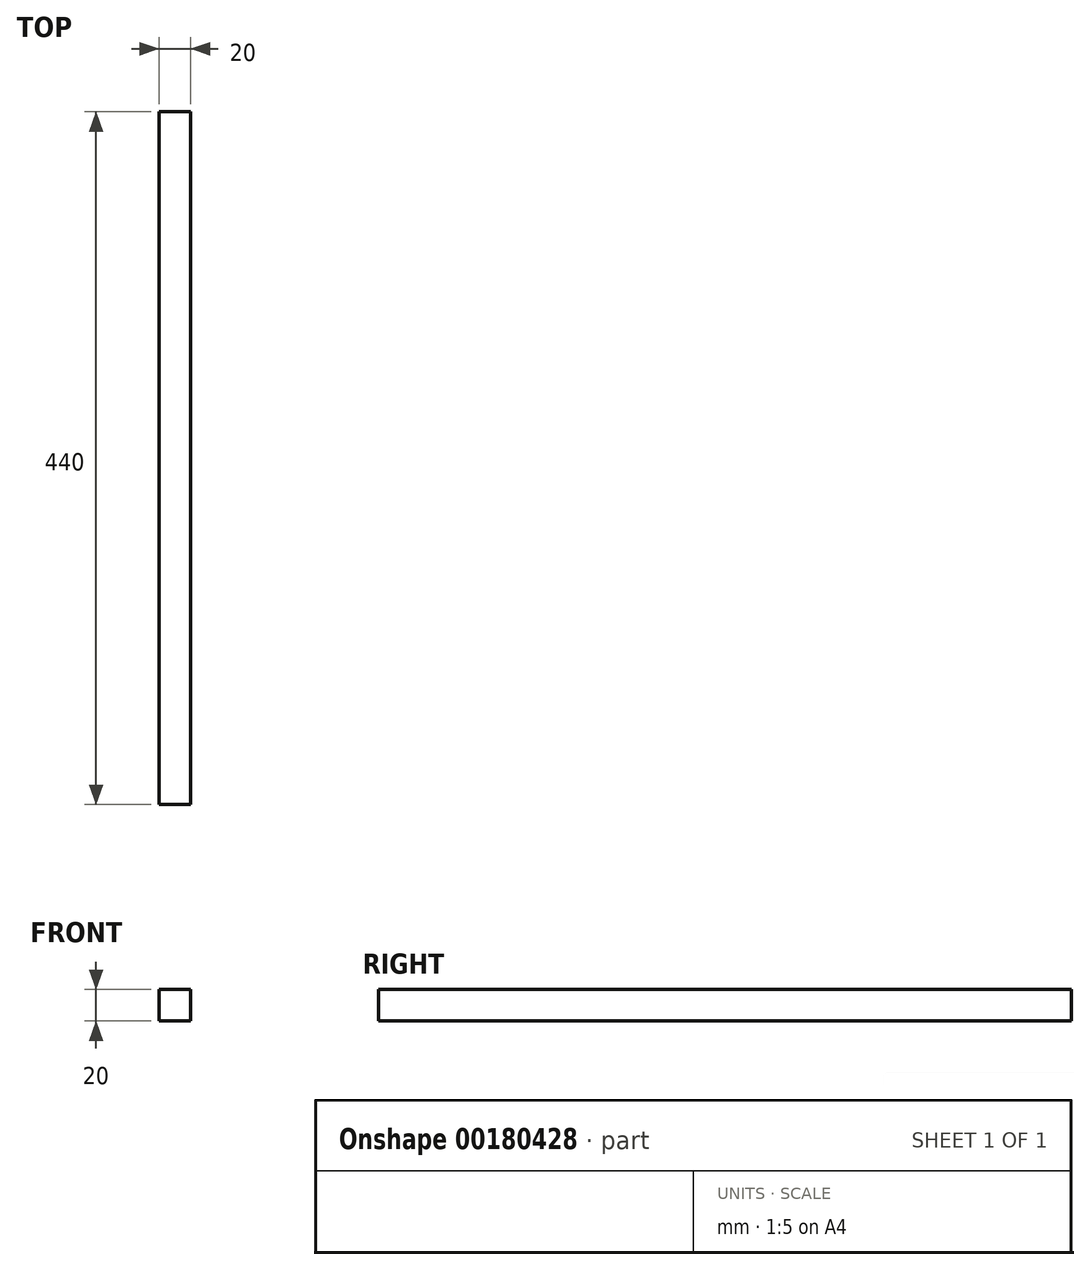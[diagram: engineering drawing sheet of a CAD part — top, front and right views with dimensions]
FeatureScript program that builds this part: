
annotation { "Feature Type Name" : "Feature", "Feature Type Description" : "" }
export const myFeature = defineFeature(function(context is Context, id is Id, definition is map)
    precondition{}
    {
        {
            var Q0;
            Q0=qCreatedBy(makeId("Front.planeOp"),FACE);
            var sketch = newSketch(context, id + "F0", { "sketchPlane" : qUnion([Q0])});
            skLineSegment(sketch, "E0.bottom", {"start": v(-500.23, -287.88) * mm, "end": v(-480.23, -287.88) * mm});
            skLineSegment(sketch, "E0.top", {"start": v(-500.23, -267.88) * mm, "end": v(-480.23, -267.88) * mm});
            skLineSegment(sketch, "E0.left", {"start": v(-500.23, -287.88) * mm, "end": v(-500.23, -267.88) * mm});
            skLineSegment(sketch, "E0.right", {"start": v(-480.23, -287.88) * mm, "end": v(-480.23, -267.88) * mm});
            skSolve(sketch);
        }
        {
            var Q0;
            Q0=makeQuery(id+"F0.imprint","IMPRINT",FACE,{"disambiguationData":[TD([[makeQuery(id+"F0.imprint","IMPRINT",EDGE,{"derivedFrom":sQuery(id+"F0.wireOp",EDGE,"E0.bottom")}),1.0]])]});
            extrude(context, id + "F1", {"entities" : qUnion([Q0]), "depth" : 440 * mm});
        }
    });
